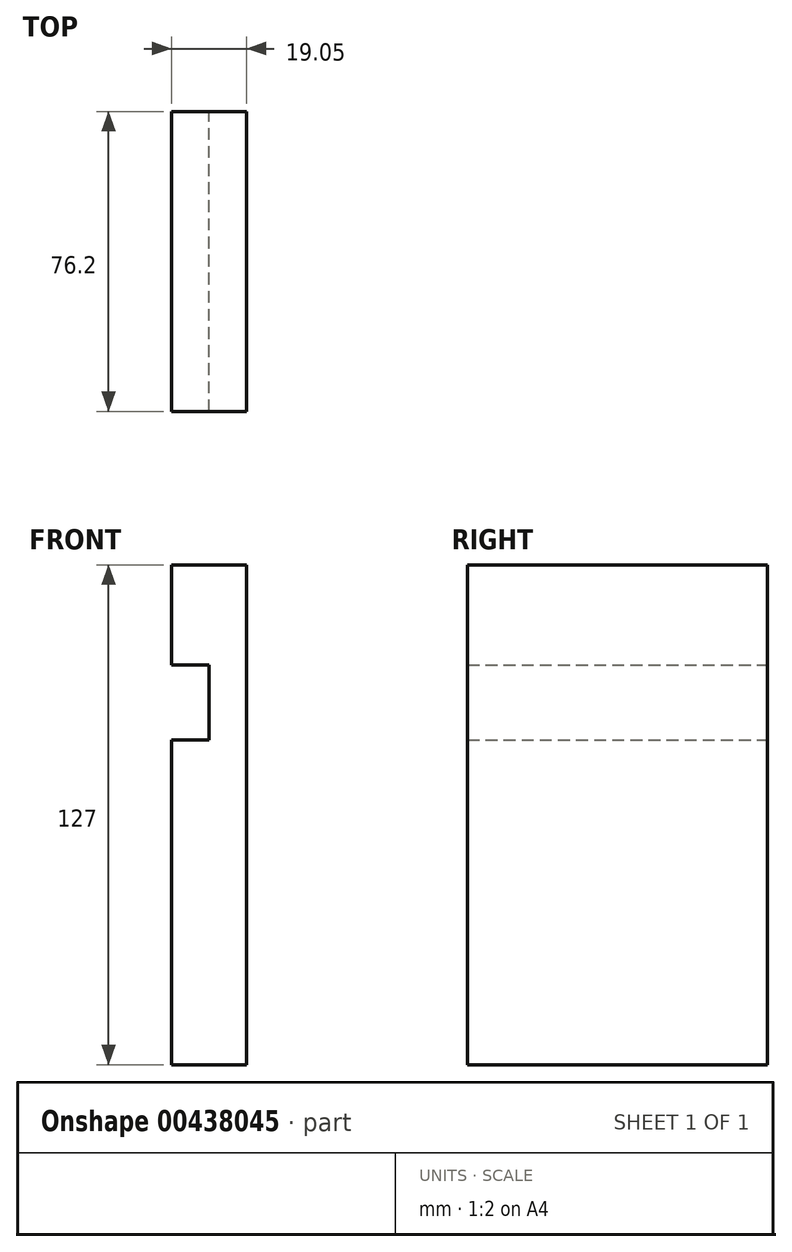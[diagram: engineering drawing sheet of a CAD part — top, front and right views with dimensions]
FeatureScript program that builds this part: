
annotation { "Feature Type Name" : "Feature", "Feature Type Description" : "" }
export const myFeature = defineFeature(function(context is Context, id is Id, definition is map)
    precondition{}
    {
        {
            var Q0;
            Q0=qCreatedBy(makeId("Front.planeOp"),FACE);
            var sketch = newSketch(context, id + "F0", { "sketchPlane" : qUnion([Q0])});
            skLineSegment(sketch, "E0", {"start": v(-19.05, 0) * mm, "end": v(0, 0) * mm});
            skLineSegment(sketch, "E1", {"start": v(0, 0) * mm, "end": v(0, 127) * mm});
            skLineSegment(sketch, "E2", {"start": v(0, 127) * mm, "end": v(-19.05, 127) * mm});
            skLineSegment(sketch, "E3", {"start": v(-19.05, 127) * mm, "end": v(-19.05, 101.6) * mm});
            skLineSegment(sketch, "E4", {"start": v(-19.05, 101.6) * mm, "end": v(-9.52, 101.6) * mm});
            skLineSegment(sketch, "E5", {"start": v(-9.52, 101.6) * mm, "end": v(-9.52, 82.55) * mm});
            skLineSegment(sketch, "E6", {"start": v(-9.52, 82.55) * mm, "end": v(-19.05, 82.55) * mm});
            skLineSegment(sketch, "E7", {"start": v(-19.05, 82.55) * mm, "end": v(-19.05, 0) * mm});
            skSolve(sketch);
        }
        {
            var Q0;
            Q0=makeQuery(id+"F0.imprint","IMPRINT",FACE,{"disambiguationData":[TD([[makeQuery(id+"F0.imprint","IMPRINT",EDGE,{"derivedFrom":sQuery(id+"F0.wireOp",EDGE,"E0")}),1.0]])]});
            extrude(context, id + "F1", {"entities" : qUnion([Q0]), "depth" : 76.2 * mm});
        }
    });
